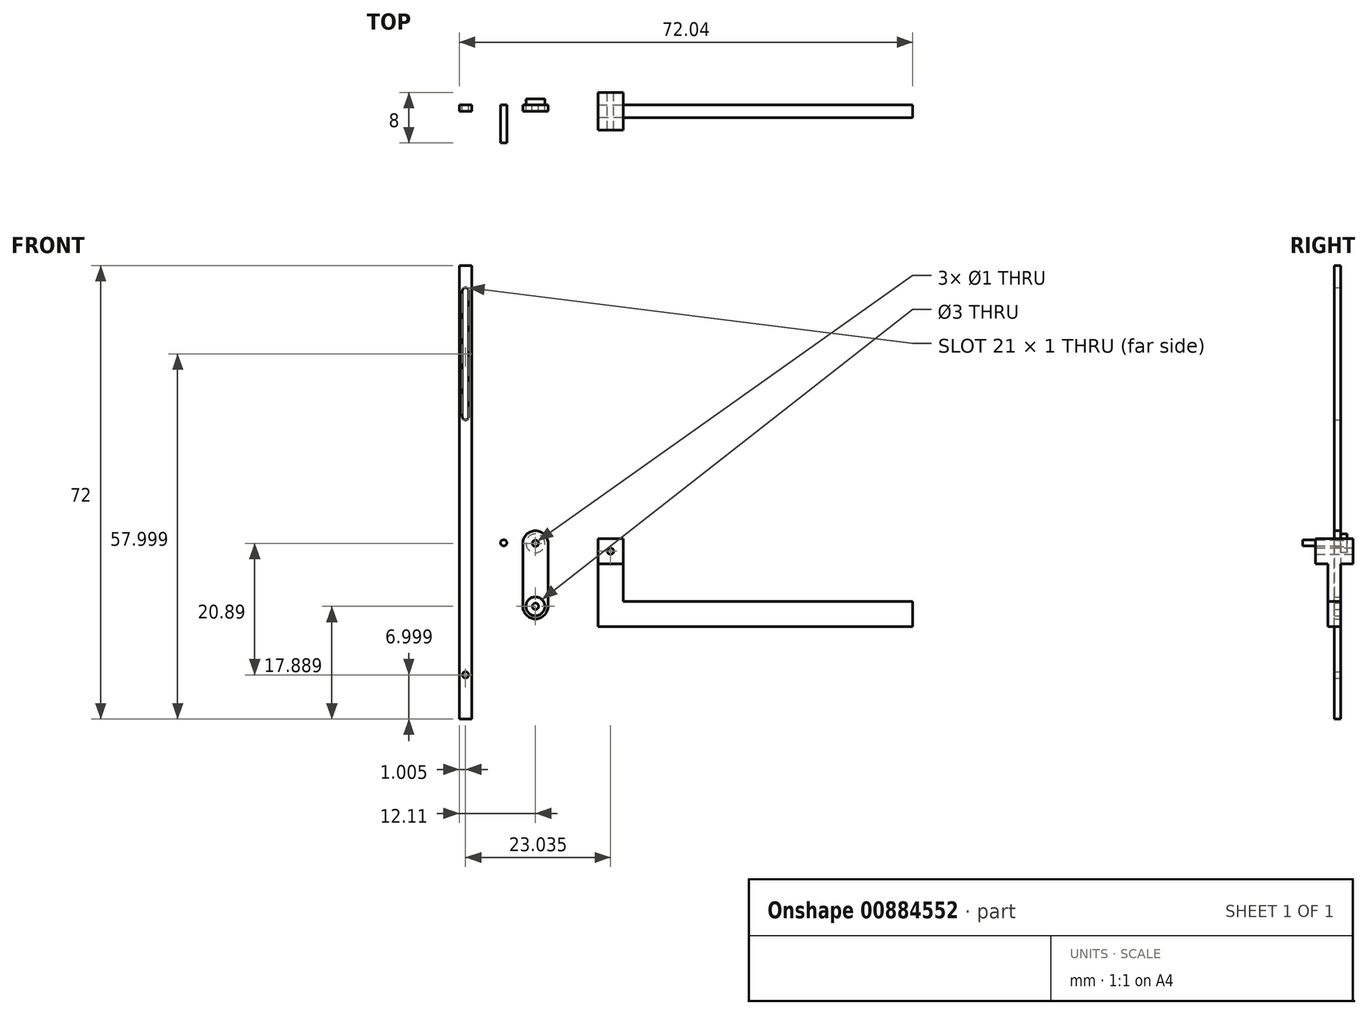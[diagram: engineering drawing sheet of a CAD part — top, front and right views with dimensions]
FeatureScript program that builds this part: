
annotation { "Feature Type Name" : "Feature", "Feature Type Description" : "" }
export const myFeature = defineFeature(function(context is Context, id is Id, definition is map)
    precondition{}
    {
        {
            var Q0;
            Q0=qCreatedBy(makeId("Front.planeOp"),FACE);
            var sketch = newSketch(context, id + "F0", { "sketchPlane" : qUnion([Q0])});
            skLineSegment(sketch, "E0.bottom", {"start": v(0, 0) * mm, "end": v(52, 0) * mm});
            skLineSegment(sketch, "E0.top", {"start": v(2, 4) * mm, "end": v(52, 4) * mm});
            skLineSegment(sketch, "E0.left", {"start": v(0, 0) * mm, "end": v(0, 4) * mm, "construction": true});
            skLineSegment(sketch, "E0.right", {"start": v(52, 0) * mm, "end": v(52, 4) * mm});
            skLineSegment(sketch, "E1.bottom", {"start": v(-2, 14) * mm, "end": v(2, 14) * mm});
            skLineSegment(sketch, "E1.right", {"start": v(2, 14) * mm, "end": v(2, 4) * mm});
            skPoint(sketch, "E1.middle", {"position": v(0, 0) * mm});
            skLineSegment(sketch, "E2", {"start": v(2, 0) * mm, "end": v(-2, 0) * mm});
            skLineSegment(sketch, "E3", {"start": v(-2, 0) * mm, "end": v(-2, 14) * mm});
            skLineSegment(sketch, "E4", {"start": v(0, 4) * mm, "end": v(0, 14) * mm, "construction": true});
            skLineSegment(sketch, "E5", {"start": v(52, 2) * mm, "end": v(-2, 2) * mm, "construction": true});
            skLineSegment(sketch, "E6.bottom", {"start": v(52, 4) * mm, "end": v(50, 4) * mm});
            skLineSegment(sketch, "E6.top", {"start": v(52, 0) * mm, "end": v(50, 0) * mm});
            skLineSegment(sketch, "E6.left", {"start": v(52, 4) * mm, "end": v(52, 0) * mm});
            skLineSegment(sketch, "E7", {"start": v(50, 4) * mm, "end": v(50, 0) * mm, "construction": true});
            skLineSegment(sketch, "E8.left", {"start": v(-2, 14) * mm, "end": v(-2, 12) * mm});
            skLineSegment(sketch, "E8.right", {"start": v(2, 14) * mm, "end": v(2, 12) * mm});
            skLineSegment(sketch, "E9", {"start": v(-2, 12) * mm, "end": v(2, 12) * mm, "construction": true});
            skCircle(sketch, "E10", {"center": v(0, 12) * mm, "radius": 0.5 * mm});
            skCircle(sketch, "E11", {"center": v(50, 2) * mm, "radius": 0.5 * mm});
            skLineSegment(sketch, "E12.bottom", {"start": v(52, 4) * mm, "end": v(48, 4) * mm, "construction": true});
            skLineSegment(sketch, "E12.top", {"start": v(52, 0) * mm, "end": v(48, 0) * mm, "construction": true});
            skLineSegment(sketch, "E12.left", {"start": v(52, 4) * mm, "end": v(52, 0) * mm, "construction": true});
            skLineSegment(sketch, "E12.right", {"start": v(48, 4) * mm, "end": v(48, 0) * mm, "construction": true});
            skLineSegment(sketch, "E13.bottom", {"start": v(-2, 14) * mm, "end": v(2, 14) * mm, "construction": true});
            skLineSegment(sketch, "E13.top", {"start": v(-2, 10) * mm, "end": v(2, 10) * mm, "construction": true});
            skLineSegment(sketch, "E13.left", {"start": v(-2, 14) * mm, "end": v(-2, 10) * mm, "construction": true});
            skLineSegment(sketch, "E13.right", {"start": v(2, 14) * mm, "end": v(2, 10) * mm, "construction": true});
            skLineSegment(sketch, "E14", {"start": v(48, 4) * mm, "end": v(48, 0) * mm});
            skLineSegment(sketch, "E15", {"start": v(-2, 10) * mm, "end": v(2, 10) * mm});
            skSolve(sketch);
        }
        {
            var Q0;
            {var subQ1=sQuery(id+"F0.wireOp",EDGE,"E0.bottom");Q0=makeQuery(id+"F0.imprint","IMPRINT",FACE,{"disambiguationData":[TD([[makeQuery(id+"F0.imprint","IMPRINT",EDGE,{"derivedFrom":subQ1}),1.0]])]});}
            var Q1;
            Q1=makeQuery(id+"F0.imprint","IMPRINT",FACE,{"disambiguationData":[TD([[makeQuery(id+"F0.imprint","IMPRINT",EDGE,{"derivedFrom":sQuery(id+"F0.wireOp",EDGE,"E1.bottom")}),-1.0]])]});
            extrude(context, id + "F1", {"entities" : qUnion([Q0, Q1]), "depth" : 2 * mm, "offsetDistance" : 25 * mm});
        }
        {
            var Q0;
            Q0=makeQuery(id+"F0.imprint","IMPRINT",FACE,{"disambiguationData":[TD([[makeQuery(id+"F0.imprint","IMPRINT",EDGE,{"derivedFrom":sQuery(id+"F0.wireOp",EDGE,"E1.bottom")}),-1.0]])]});
            var Q1;
            {var subQ1=sQuery(id+"F0.wireOp",EDGE,"E6.bottom");Q1=makeQuery(id+"F0.imprint","IMPRINT",FACE,{"disambiguationData":[TD([[makeQuery(id+"F0.imprint","IMPRINT",EDGE,{"derivedFrom":subQ1}),1.0]])]});}
            extrude(context, id + "F2", {"entities" : qUnion([Q0, Q1]), "operationType" : NewBodyOperationType.ADD, "oppositeDirection" : true, "depth" : 2 * mm, "offsetDistance" : 25 * mm});
        }
        {
            var Q0;
            {var subQ5=sQuery(id+"F0.wireOp",EDGE,"E14");Q0=makeQuery(id+"F0.imprint","IMPRINT",FACE,{"disambiguationData":[TD([[makeQuery(id+"F0.imprint","IMPRINT",EDGE,{"derivedFrom":subQ5}),-1.0]])]});}
            var Q1;
            {var subQ1=sQuery(id+"F0.wireOp",EDGE,"E6.bottom");Q1=makeQuery(id+"F0.imprint","IMPRINT",FACE,{"disambiguationData":[TD([[makeQuery(id+"F0.imprint","IMPRINT",EDGE,{"derivedFrom":subQ1}),1.0]])]});}
            var Q2;
            Q2=makeQuery(id+"F0.imprint","IMPRINT",FACE,{"disambiguationData":[TD([[makeQuery(id+"F0.imprint","IMPRINT",EDGE,{"derivedFrom":sQuery(id+"F0.wireOp",EDGE,"E1.bottom")}),-1.0]])]});
            extrude(context, id + "F3", {"entities" : qUnion([Q0, Q1, Q2]), "depth" : 2 * mm, "offsetDistance" : 25 * mm});
        }
        {
            var Q0;
            Q0=makeQuery(id+"F0.imprint","IMPRINT",FACE,{"disambiguationData":[TD([[makeQuery(id+"F0.imprint","IMPRINT",EDGE,{"derivedFrom":sQuery(id+"F0.wireOp",EDGE,"E1.bottom")}),-1.0]])]});
            var Q1;
            {var subQ1=sQuery(id+"F0.wireOp",EDGE,"E6.bottom");Q1=makeQuery(id+"F0.imprint","IMPRINT",FACE,{"disambiguationData":[TD([[makeQuery(id+"F0.imprint","IMPRINT",EDGE,{"derivedFrom":subQ1}),1.0]])]});}
            extrude(context, id + "F4", {"entities" : qUnion([Q0, Q1]), "operationType" : NewBodyOperationType.ADD, "depth" : 4 * mm, "offsetDistance" : 25 * mm, "hasSecondDirection" : true, "secondDirectionOppositeDirection" : true, "secondDirectionDepth" : 2 * mm});
        }
        {
            var Q0;
            Q0=qCreatedBy(makeId("Front.planeOp"),FACE);
            var sketch = newSketch(context, id + "F5", { "sketchPlane" : qUnion([Q0])});
            skLineSegment(sketch, "E16.bottom", {"start": v(-11.93, 15.24) * mm, "end": v(-11.93, 15.24) * mm});
            skLineSegment(sketch, "E16.left", {"start": v(-13.93, 13.24) * mm, "end": v(-13.93, 8.24) * mm});
            skLineSegment(sketch, "E16.right", {"start": v(-9.93, 13.24) * mm, "end": v(-9.93, 8.24) * mm});
            skLineSegment(sketch, "E17", {"start": v(-11.93, 15.24) * mm, "end": v(-11.93, 8.24) * mm, "construction": true});
            skLineSegment(sketch, "E18.top", {"start": v(-13.93, 13.24) * mm, "end": v(-9.93, 13.24) * mm, "construction": true});
            skLineSegment(sketch, "E19", {"start": v(-13.93, 8.24) * mm, "end": v(-9.93, 8.24) * mm});
            skPoint(sketch, "E20.visualSharp", {"position": v(-13.93, 15.24) * mm});
            skArc(sketch, "E20.filletArc", {"start": v(-11.93, 15.24) * mm, "mid": v(-13.34, 14.65) * mm, "end": v(-13.93, 13.24) * mm});
            skPoint(sketch, "E21.visualSharp", {"position": v(-9.93, 15.24) * mm});
            skArc(sketch, "E21.filletArc", {"start": v(-9.93, 13.24) * mm, "mid": v(-10.52, 14.65) * mm, "end": v(-11.93, 15.24) * mm});
            skCircle(sketch, "E22", {"center": v(-11.93, 13.24) * mm, "radius": 0.5 * mm});
            skLineSegment(sketch, "E23.MirrorCS", {"start": v(-13.93, 3.24) * mm, "end": v(-13.93, 8.24) * mm});
            skArc(sketch, "E24.MirrorCS", {"start": v(-11.93, 1.24) * mm, "mid": v(-13.34, 1.82) * mm, "end": v(-13.93, 3.24) * mm});
            skLineSegment(sketch, "E25.MirrorCS", {"start": v(-11.93, 1.24) * mm, "end": v(-11.93, 1.24) * mm});
            skArc(sketch, "E26.MirrorCS", {"start": v(-9.93, 3.24) * mm, "mid": v(-10.52, 1.82) * mm, "end": v(-11.93, 1.24) * mm});
            skLineSegment(sketch, "E27.MirrorCS", {"start": v(-9.93, 3.24) * mm, "end": v(-9.93, 8.24) * mm});
            skCircle(sketch, "E28.MirrorC", {"center": v(-11.93, 3.24) * mm, "radius": 0.5 * mm});
            skCircle(sketch, "E29.0", {"center": v(-11.93, 13.24) * mm, "radius": 1.5 * mm});
            skCircle(sketch, "E30.MirrorC", {"center": v(-11.93, 3.24) * mm, "radius": 1.5 * mm});
            skSolve(sketch);
        }
        {
            var Q0;
            Q0=makeQuery(id+"F5.imprint","IMPRINT",FACE,{"disambiguationData":[TD([[makeQuery(id+"F5.imprint","IMPRINT",EDGE,{"derivedFrom":sQuery(id+"F5.wireOp",EDGE,"E16.left")}),1.0]])]});
            var Q1;
            Q1=makeQuery(id+"F5.imprint","IMPRINT",FACE,{"disambiguationData":[TD([[makeQuery(id+"F5.imprint","IMPRINT",EDGE,{"derivedFrom":sQuery(id+"F5.wireOp",EDGE,"E19")}),-1.0]])]});
            var Q2;
            Q2=makeQuery(id+"F5.imprint","IMPRINT",FACE,{"disambiguationData":[TD([[makeQuery(id+"F5.imprint","IMPRINT",EDGE,{"derivedFrom":sQuery(id+"F5.wireOp",EDGE,"E28.MirrorC")}),1.0]])]});
            var Q3;
            Q3=makeQuery(id+"F5.imprint","IMPRINT",FACE,{"disambiguationData":[TD([[makeQuery(id+"F5.imprint","IMPRINT",EDGE,{"derivedFrom":sQuery(id+"F5.wireOp",EDGE,"E22")}),-1.0]])]});
            extrude(context, id + "F6", {"entities" : qUnion([Q0, Q1, Q2, Q3]), "depth" : 1 * mm, "offsetDistance" : 25 * mm});
        }
        {
            var Q0;
            Q0=makeQuery(id+"F5.imprint","IMPRINT",FACE,{"disambiguationData":[TD([[makeQuery(id+"F5.imprint","IMPRINT",EDGE,{"derivedFrom":sQuery(id+"F5.wireOp",EDGE,"E22")}),-1.0]])]});
            extrude(context, id + "F7", {"entities" : qUnion([Q0]), "operationType" : NewBodyOperationType.ADD, "oppositeDirection" : true, "depth" : 1 * mm, "offsetDistance" : 25 * mm});
        }
        {
            var Q0;
            Q0=qCreatedBy(makeId("Front.planeOp"),FACE);
            var sketch = newSketch(context, id + "F8", { "sketchPlane" : qUnion([Q0])});
            skCircle(sketch, "E31", {"center": v(-16.96, 13.32) * mm, "radius": 0.5 * mm});
            skSolve(sketch);
        }
        {
            var Q0;
            Q0=makeQuery(id+"F8.imprint","IMPRINT",FACE,{"disambiguationData":[TD([[makeQuery(id+"F8.imprint","IMPRINT",EDGE,{"derivedFrom":sQuery(id+"F8.wireOp",EDGE,"E31")}),1.0]])]});
            extrude(context, id + "F9", {"entities" : qUnion([Q0]), "depth" : 6 * mm, "offsetDistance" : 25 * mm});
        }
        {
            var Q0;
            Q0=qCreatedBy(makeId("Front.planeOp"),FACE);
            var sketch = newSketch(context, id + "F10", { "sketchPlane" : qUnion([Q0])});
            skLineSegment(sketch, "E32.bottom", {"start": v(-24.04, -14.65) * mm, "end": v(-22.04, -14.65) * mm});
            skLineSegment(sketch, "E32.top", {"start": v(-24.04, 57.35) * mm, "end": v(-22.04, 57.35) * mm});
            skLineSegment(sketch, "E32.left", {"start": v(-24.04, -14.65) * mm, "end": v(-24.04, 57.35) * mm});
            skLineSegment(sketch, "E32.right", {"start": v(-22.04, -14.65) * mm, "end": v(-22.04, 57.35) * mm});
            skPoint(sketch, "E32.middle", {"position": v(-23.04, 21.35) * mm});
            skLineSegment(sketch, "E33.bottom", {"start": v(-24.04, 57.35) * mm, "end": v(-22.04, 57.35) * mm, "construction": true});
            skLineSegment(sketch, "E33.top", {"start": v(-24.04, 33.35) * mm, "end": v(-22.04, 33.35) * mm, "construction": true});
            skLineSegment(sketch, "E33.left", {"start": v(-24.04, 57.35) * mm, "end": v(-24.04, 33.35) * mm, "construction": true});
            skLineSegment(sketch, "E33.right", {"start": v(-22.04, 57.35) * mm, "end": v(-22.04, 33.35) * mm, "construction": true});
            skArc(sketch, "E34", {"start": v(-23.54, 33.35) * mm, "mid": v(-23.04, 32.85) * mm, "end": v(-22.54, 33.35) * mm});
            skLineSegment(sketch, "E35", {"start": v(-23.04, 57.35) * mm, "end": v(-23.04, 33.35) * mm, "construction": true});
            skArc(sketch, "E36", {"start": v(-22.54, 53.35) * mm, "mid": v(-23.04, 53.85) * mm, "end": v(-23.54, 53.35) * mm});
            skLineSegment(sketch, "E37", {"start": v(-23.54, 53.35) * mm, "end": v(-23.54, 33.35) * mm});
            skLineSegment(sketch, "E38", {"start": v(-22.54, 33.35) * mm, "end": v(-22.54, 53.35) * mm});
            skLineSegment(sketch, "E39.bottom", {"start": v(-24.04, -14.65) * mm, "end": v(-22.04, -14.65) * mm, "construction": true});
            skLineSegment(sketch, "E39.top", {"start": v(-24.04, -7.65) * mm, "end": v(-22.04, -7.65) * mm, "construction": true});
            skLineSegment(sketch, "E39.left", {"start": v(-24.04, -14.65) * mm, "end": v(-24.04, -7.65) * mm, "construction": true});
            skLineSegment(sketch, "E39.right", {"start": v(-22.04, -14.65) * mm, "end": v(-22.04, -7.65) * mm, "construction": true});
            skCircle(sketch, "E40", {"center": v(-23.04, -7.65) * mm, "radius": 0.5 * mm});
            skPoint(sketch, "E40.perimeterSnap0", {"position": v(-23.04, -7.65) * mm});
            skSolve(sketch);
        }
        {
            var Q0;
            Q0=makeQuery(id+"F10.imprint","IMPRINT",FACE,{"disambiguationData":[TD([[makeQuery(id+"F10.imprint","IMPRINT",EDGE,{"derivedFrom":sQuery(id+"F10.wireOp",EDGE,"E32.bottom")}),1.0]])]});
            extrude(context, id + "F11", {"entities" : qUnion([Q0]), "depth" : 1 * mm, "offsetDistance" : 25 * mm});
        }
    });
